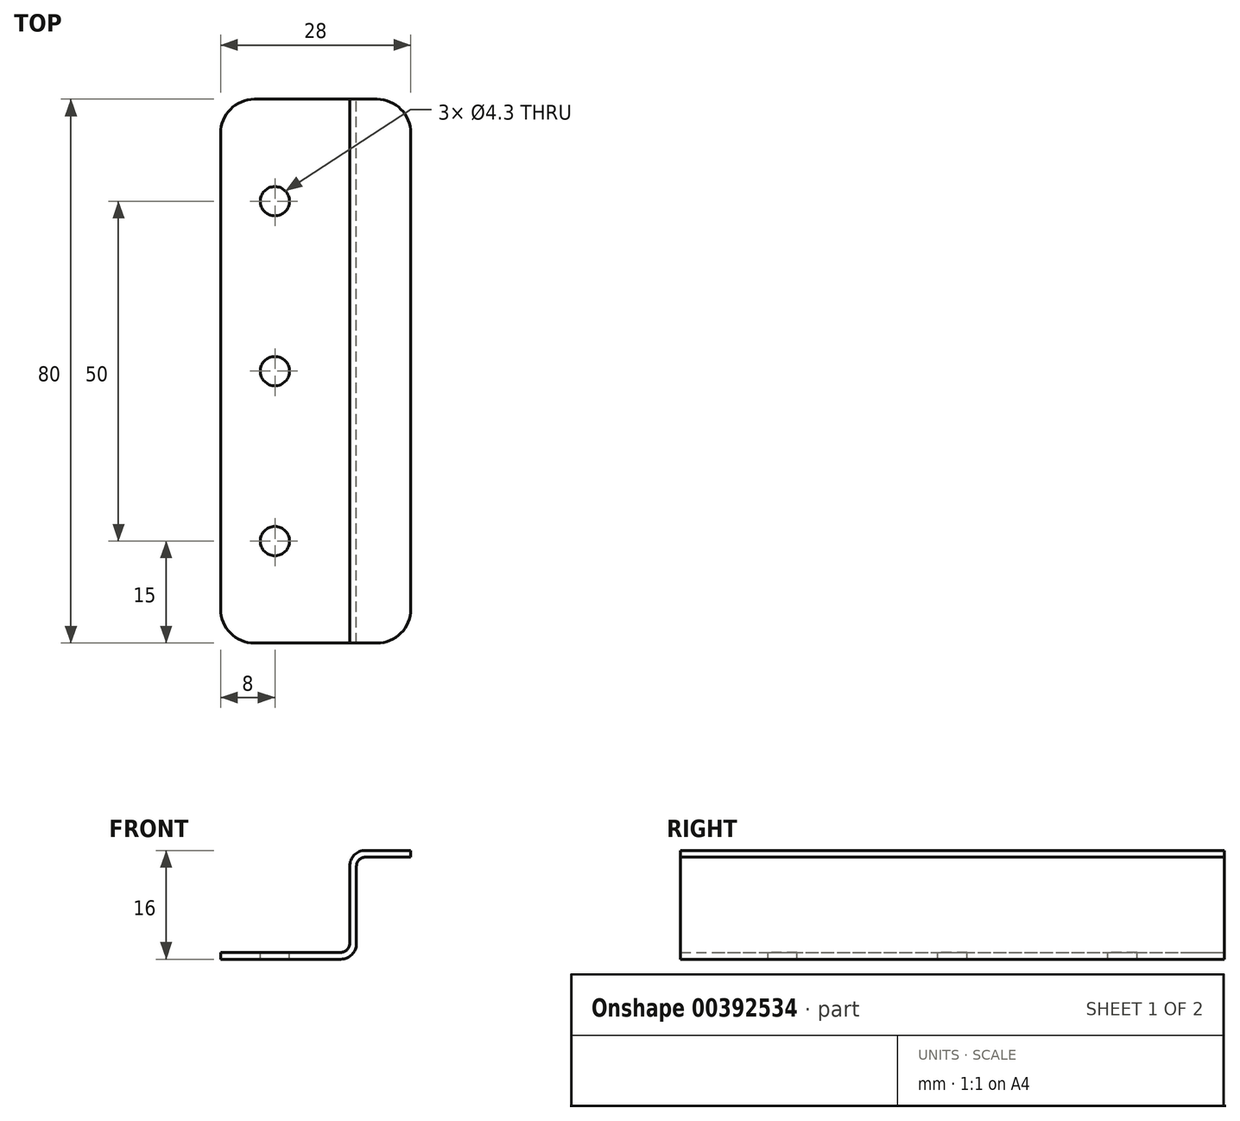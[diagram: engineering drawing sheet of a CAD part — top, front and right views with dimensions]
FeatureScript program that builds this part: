
annotation { "Feature Type Name" : "Feature", "Feature Type Description" : "" }
export const myFeature = defineFeature(function(context is Context, id is Id, definition is map)
    precondition{}
    {
        {
            var Q0;
            Q0=qCreatedBy(makeId("Front.planeOp"),FACE);
            var sketch = newSketch(context, id + "F0", { "sketchPlane" : qUnion([Q0])});
            skLineSegment(sketch, "E0", {"start": v(0, 0) * mm, "end": v(17.7, 0) * mm});
            skLineSegment(sketch, "E1", {"start": v(20, 2.3) * mm, "end": v(20, 13.7) * mm});
            skLineSegment(sketch, "E2", {"start": v(21.3, 15) * mm, "end": v(28, 15) * mm});
            skLineSegment(sketch, "E3", {"start": v(28, 15) * mm, "end": v(28, 16) * mm});
            skLineSegment(sketch, "E4", {"start": v(28, 16) * mm, "end": v(21.3, 16) * mm});
            skLineSegment(sketch, "E5", {"start": v(19, 13.7) * mm, "end": v(19, 2.3) * mm});
            skLineSegment(sketch, "E6", {"start": v(17.7, 1) * mm, "end": v(0, 1) * mm});
            skLineSegment(sketch, "E7", {"start": v(0, 1) * mm, "end": v(0, 0) * mm});
            skPoint(sketch, "E8.visualSharp", {"position": v(19, 1) * mm});
            skArc(sketch, "E8.filletArc", {"start": v(17.7, 1) * mm, "mid": v(18.62, 1.38) * mm, "end": v(19, 2.3) * mm});
            skPoint(sketch, "E9.visualSharp", {"position": v(20, 15) * mm});
            skArc(sketch, "E9.filletArc", {"start": v(21.3, 15) * mm, "mid": v(20.38, 14.62) * mm, "end": v(20, 13.7) * mm});
            skPoint(sketch, "E10.visualSharp", {"position": v(20, 0) * mm});
            skArc(sketch, "E10.filletArc", {"start": v(17.7, 0) * mm, "mid": v(19.33, 0.67) * mm, "end": v(20, 2.3) * mm});
            skPoint(sketch, "E11.visualSharp", {"position": v(19, 16) * mm});
            skArc(sketch, "E11.filletArc", {"start": v(21.3, 16) * mm, "mid": v(19.67, 15.33) * mm, "end": v(19, 13.7) * mm});
            skSolve(sketch);
        }
        {
            var Q0;
            Q0=makeQuery(id+"F0.imprint","IMPRINT",FACE,{"disambiguationData":[TD([[makeQuery(id+"F0.imprint","IMPRINT",EDGE,{"derivedFrom":sQuery(id+"F0.wireOp",EDGE,"E0")}),1.0]])]});
            extrude(context, id + "F1", {"entities" : qUnion([Q0]), "endBound" : BoundingType.SYMMETRIC, "depth" : 80 * mm});
        }
        {
            var Q0;
            Q0=makeQuery(id+"F1.opExtrude","SWEPT_FACE",FACE,{"disambiguationData":[OSD([sQuery(id+"F0.wireOp",EDGE,"E6")])]});
            var sketch = newSketch(context, id + "F2", { "sketchPlane" : qUnion([Q0])});
            skCircle(sketch, "E12", {"center": v(8, 0) * mm, "radius": 2.15 * mm});
            skCircle(sketch, "E13.0.1.0", {"center": v(8, 25) * mm, "radius": 2.15 * mm});
            skLineSegment(sketch, "E13.direction1", {"start": v(8, 0) * mm, "end": v(33, 0) * mm, "construction": true});
            skLineSegment(sketch, "E13.direction2", {"start": v(8, 0) * mm, "end": v(8, 25) * mm, "construction": true});
            skCircle(sketch, "E14.0.1.0", {"center": v(8, -25) * mm, "radius": 2.15 * mm});
            skLineSegment(sketch, "E14.direction2", {"start": v(8, 0) * mm, "end": v(8, -25) * mm, "construction": true});
            skSolve(sketch);
        }
        {
            var Q0;
            Q0=makeQuery(id+"F2.imprint","IMPRINT",FACE,{"disambiguationData":[TD([[makeQuery(id+"F2.imprint","IMPRINT",EDGE,{"derivedFrom":sQuery(id+"F2.wireOp",EDGE,"E13.0.1.0")}),1.0]])]});
            var Q1;
            Q1=makeQuery(id+"F2.imprint","IMPRINT",FACE,{"disambiguationData":[TD([[makeQuery(id+"F2.imprint","IMPRINT",EDGE,{"derivedFrom":sQuery(id+"F2.wireOp",EDGE,"E12")}),1.0]])]});
            var Q2;
            Q2=makeQuery(id+"F2.imprint","IMPRINT",FACE,{"disambiguationData":[TD([[makeQuery(id+"F2.imprint","IMPRINT",EDGE,{"derivedFrom":sQuery(id+"F2.wireOp",EDGE,"E14.0.1.0")}),1.0]])]});
            extrude(context, id + "F3", {"entities" : qUnion([Q0, Q1, Q2]), "operationType" : NewBodyOperationType.REMOVE, "endBound" : BoundingType.UP_TO_NEXT, "oppositeDirection" : true, "depth" : 25 * mm});
        }
        {
            var Q0;
            Q0=makeQuery(id+"F1.opExtrude","CAP_EDGE",EDGE,{"disambiguationData":[OSD([sQuery(id+"F0.wireOp",EDGE,"E7")])],"isStart":true});
            var Q1;
            Q1=makeQuery(id+"F1.opExtrude","CAP_EDGE",EDGE,{"disambiguationData":[OSD([sQuery(id+"F0.wireOp",EDGE,"E7")])],"isStart":false});
            var Q2;
            Q2=makeQuery(id+"F1.opExtrude","CAP_EDGE",EDGE,{"disambiguationData":[OSD([sQuery(id+"F0.wireOp",EDGE,"E3")])],"isStart":false});
            var Q3;
            Q3=makeQuery(id+"F1.opExtrude","CAP_EDGE",EDGE,{"disambiguationData":[OSD([sQuery(id+"F0.wireOp",EDGE,"E3")])],"isStart":true});
            fillet(context, id + "F4", {"entities" : qUnion([Q0, Q1, Q2, Q3]), "radius" : 5 * mm, "tangentPropagation" : true, "allowEdgeOverflow" : false});
        }
    });
